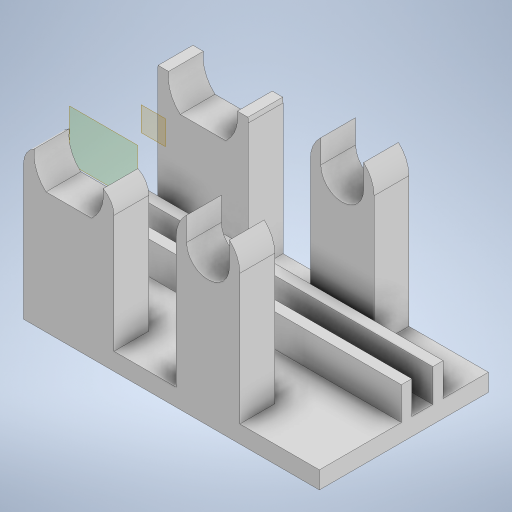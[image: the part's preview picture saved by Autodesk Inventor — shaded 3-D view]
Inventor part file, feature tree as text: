
AUTODESK INVENTOR PART (.ipt)
format: ipt  version: 2023 (Build 270158000, 158)  size: 412,672 bytes
history: native  units: mm
features: other x6, extrude x3, plane x2, sketch x2, reference x2, fillet x1, mirror x1
ambient origin geometry x8: Origin, YZ Plane, XZ Plane, XY Plane, X Axis, Y Axis, Z Axis, Center Point
bodies: Solid1 (feature_tree)
feature tree (17):
  plane  "Work Plane1"
  plane  "Work Plane2"
  sketch  "Sketch1"  dims[d0=0.1mm d1=5.0mm]
  extrude  "Extrusion1"  Depth=5.0mm
  extrude  "Extrusion2"  Depth=3.0mm
  fillet  "Fillet1"  Radius=10.0mm
  mirror  "Mirror2"
  extrude  "Extrusion3"  Depth=10.0mm TaperAngle=0.0deg
  reference  "Reference2"
  sketch  "Sketch2"  dims[d2=5.5mm d3=3.0mm d4=10.0mm d5=0.0mm d6=10.0mm d7=0.0mm d8=5.75mm d9=3.0mm d10=0.5mm d11=3.0mm d12=3.0mm d13=10.0mm d14=0.0mm]
  reference  "Reference3"
  parser-record x1  (decoder bookkeeping rows leaked as tree rows — omitted from the tree; the rows remain in map.json)
  other  "doorLockAssembly_V3.iam"
  other  "gear_V3:1"
  other  "rack_V3:1"
  other  "pinion_V3:1"
  other  "motor:2"
note: 1 file-system path scrubbed to <path> (originals preserved in map.json)
